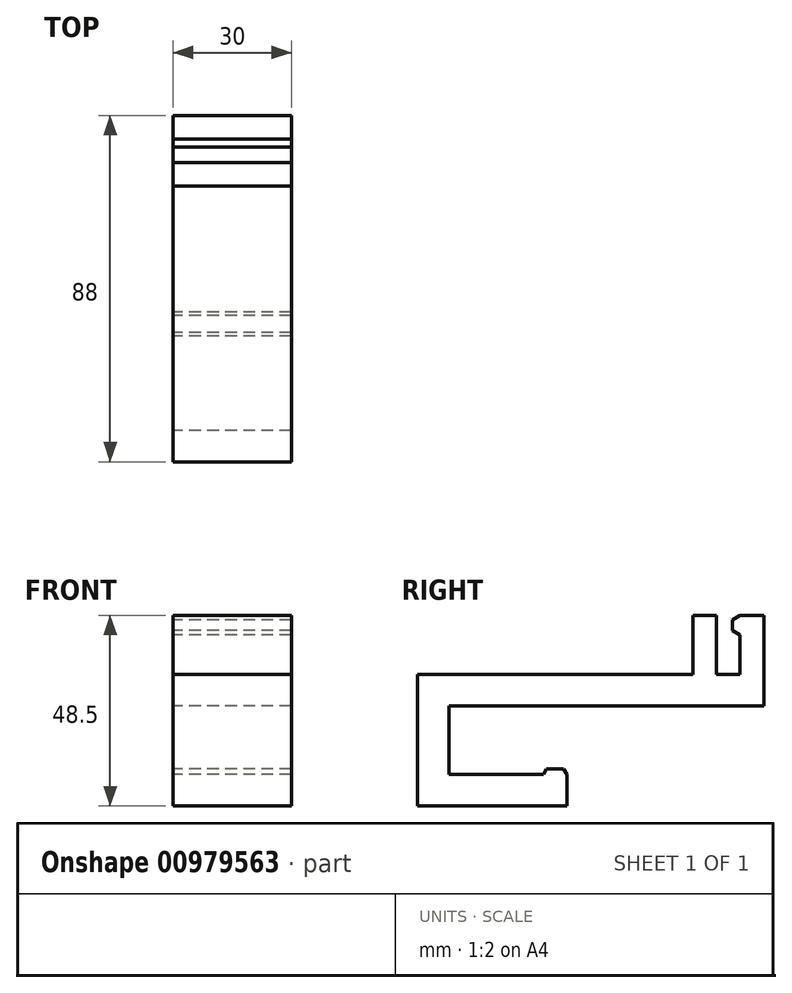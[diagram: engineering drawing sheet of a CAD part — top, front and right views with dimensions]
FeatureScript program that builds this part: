
annotation { "Feature Type Name" : "Feature", "Feature Type Description" : "" }
export const myFeature = defineFeature(function(context is Context, id is Id, definition is map)
    precondition{}
    {
        {
            var Q0;
            Q0=qCreatedBy(makeId("Right.planeOp"),FACE);
            var sketch = newSketch(context, id + "F0", { "sketchPlane" : qUnion([Q0])});
            skLineSegment(sketch, "E0", {"start": v(0, 0) * mm, "end": v(0, 33.5) * mm});
            skLineSegment(sketch, "E1", {"start": v(0, 33.5) * mm, "end": v(70, 33.5) * mm});
            skLineSegment(sketch, "E2", {"start": v(70, 33.5) * mm, "end": v(70, 48.5) * mm});
            skLineSegment(sketch, "E3", {"start": v(70, 48.5) * mm, "end": v(76, 48.5) * mm});
            skLineSegment(sketch, "E4", {"start": v(76, 48.5) * mm, "end": v(76, 33.5) * mm});
            skLineSegment(sketch, "E5", {"start": v(76, 33.5) * mm, "end": v(82, 33.5) * mm});
            skLineSegment(sketch, "E6", {"start": v(82, 33.5) * mm, "end": v(82, 43.5) * mm});
            skLineSegment(sketch, "E7", {"start": v(82, 48.5) * mm, "end": v(88, 48.5) * mm});
            skLineSegment(sketch, "E8", {"start": v(88, 48.5) * mm, "end": v(88, 25.5) * mm});
            skLineSegment(sketch, "E9", {"start": v(88, 25.5) * mm, "end": v(8, 25.5) * mm});
            skLineSegment(sketch, "E10", {"start": v(8, 25.5) * mm, "end": v(8, 8) * mm});
            skLineSegment(sketch, "E11", {"start": v(8, 8) * mm, "end": v(32, 8) * mm});
            skLineSegment(sketch, "E12", {"start": v(38, 8) * mm, "end": v(38, 0) * mm});
            skLineSegment(sketch, "E13", {"start": v(38, 0) * mm, "end": v(0, 0) * mm});
            skLineSegment(sketch, "E14", {"start": v(76, 48.5) * mm, "end": v(82, 48.5) * mm, "construction": true});
            skLineSegment(sketch, "E15", {"start": v(38, 8) * mm, "end": v(37.13, 9.5) * mm});
            skLineSegment(sketch, "E16", {"start": v(37.13, 9.5) * mm, "end": v(32.87, 9.5) * mm});
            skLineSegment(sketch, "E17", {"start": v(32.87, 9.5) * mm, "end": v(32, 8) * mm});
            skLineSegment(sketch, "E18", {"start": v(38, 8) * mm, "end": v(32, 8) * mm, "construction": true});
            skLineSegment(sketch, "E19", {"start": v(82, 48.5) * mm, "end": v(80, 47.35) * mm});
            skLineSegment(sketch, "E20", {"start": v(80, 47.35) * mm, "end": v(80, 44.65) * mm});
            skLineSegment(sketch, "E21", {"start": v(80, 44.65) * mm, "end": v(82, 43.5) * mm});
            skLineSegment(sketch, "E22", {"start": v(82, 43.5) * mm, "end": v(82, 48.5) * mm, "construction": true});
            skSolve(sketch);
        }
        {
            var Q0;
            Q0 = qSketchRegion(id + "F0", true);
            extrude(context, id + "F1", {"entities" : qUnion([Q0]), "depth" : 30 * mm, "offsetDistance" : 25 * mm});
        }
    });
